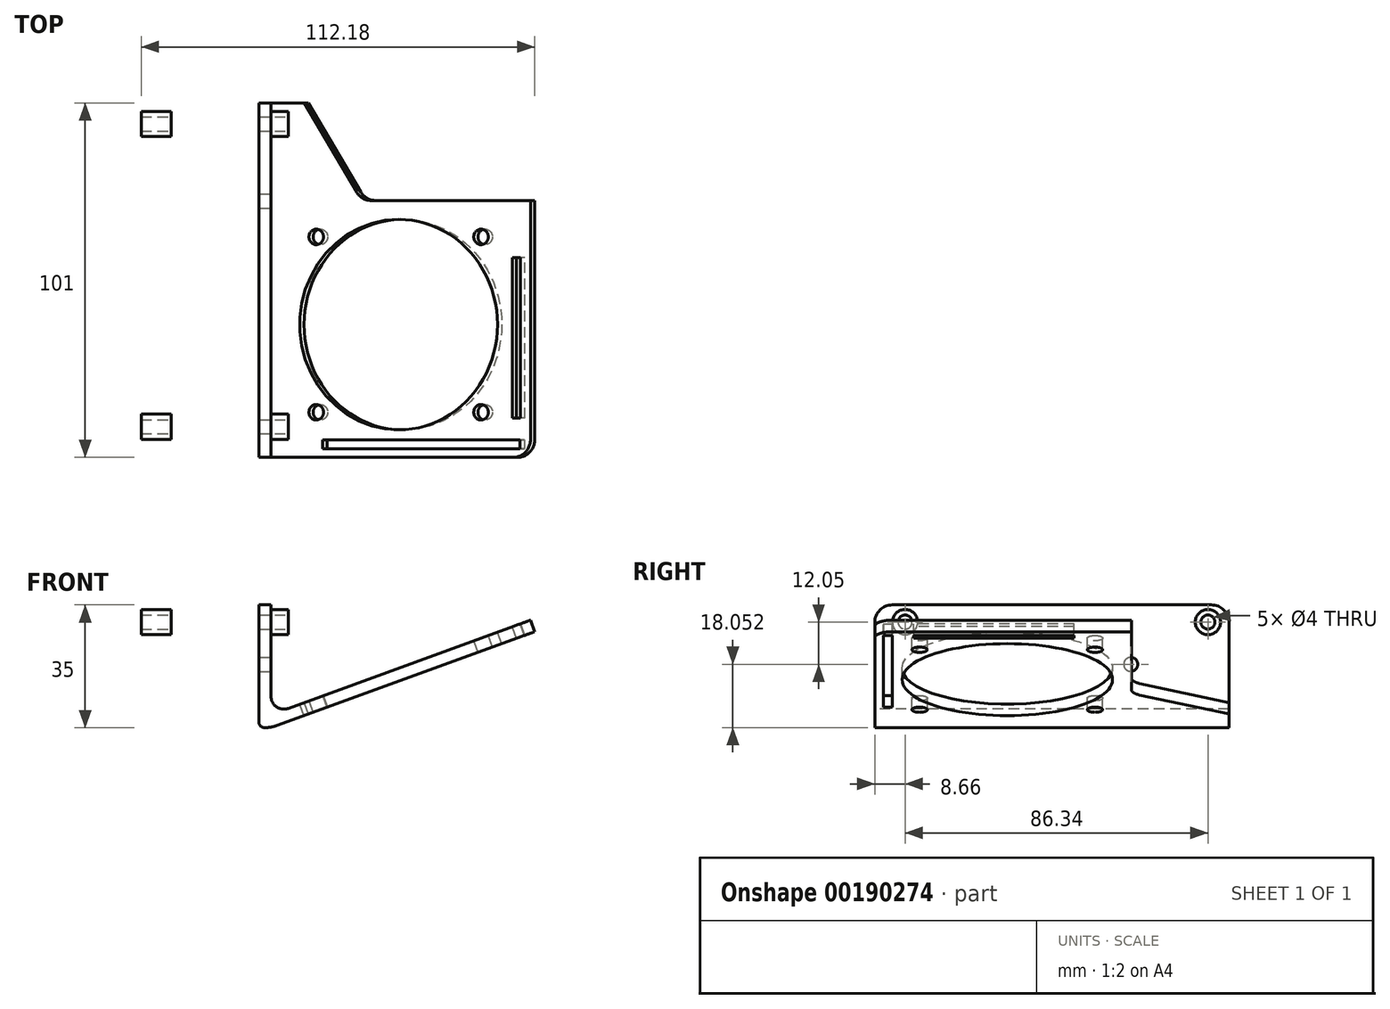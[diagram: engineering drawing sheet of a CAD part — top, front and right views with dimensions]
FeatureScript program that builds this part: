
annotation { "Feature Type Name" : "Feature", "Feature Type Description" : "" }
export const myFeature = defineFeature(function(context is Context, id is Id, definition is map)
    precondition{}
    {
        {
            var Q0;
            Q0=qCreatedBy(makeId("Front.planeOp"),FACE);
            var sketch = newSketch(context, id + "F0", { "sketchPlane" : qUnion([Q0])});
            skLineSegment(sketch, "E0.bottom", {"start": v(1.7, 0) * mm, "end": v(1.77, 0) * mm});
            skLineSegment(sketch, "E0.top", {"start": v(0, 35) * mm, "end": v(3.5, 35) * mm});
            skLineSegment(sketch, "E0.left", {"start": v(0, 1.7) * mm, "end": v(0, 35) * mm});
            skLineSegment(sketch, "E0.right", {"start": v(3.5, 8.92) * mm, "end": v(3.5, 35) * mm});
            skLineSegment(sketch, "E1", {"start": v(5.13, 0.6) * mm, "end": v(78.68, 27.36) * mm});
            skLineSegment(sketch, "E2", {"start": v(8.38, 5.5) * mm, "end": v(77.48, 30.65) * mm});
            skLineSegment(sketch, "E3", {"start": v(78.68, 27.36) * mm, "end": v(77.48, 30.65) * mm});
            skPoint(sketch, "E4.visualSharp", {"position": v(3.5, 0) * mm});
            skArc(sketch, "E4.filletArc", {"start": v(1.77, 0) * mm, "mid": v(3.47, 0.15) * mm, "end": v(5.13, 0.6) * mm});
            skPoint(sketch, "E5.visualSharp", {"position": v(0, 0) * mm});
            skArc(sketch, "E5.filletArc", {"start": v(0, 1.7) * mm, "mid": v(0.5, 0.5) * mm, "end": v(1.7, 0) * mm});
            skPoint(sketch, "E6.visualSharp", {"position": v(3.5, 3.72) * mm});
            skArc(sketch, "E6.filletArc", {"start": v(3.5, 8.92) * mm, "mid": v(5.05, 5.94) * mm, "end": v(8.38, 5.5) * mm});
            skSolve(sketch);
        }
        {
            var Q0;
            Q0=makeQuery(id+"F0.imprint","IMPRINT",FACE,{"disambiguationData":[TD([[makeQuery(id+"F0.imprint","IMPRINT",EDGE,{"derivedFrom":sQuery(id+"F0.wireOp",EDGE,"E0.bottom")}),1.0]])]});
            extrude(context, id + "F1", {"entities" : qUnion([Q0]), "oppositeDirection" : true, "depth" : 101 * mm});
        }
        {
            var Q0;
            Q0=makeQuery(id+"F1.opExtrude","SWEPT_FACE",FACE,{"disambiguationData":[OSD([sQuery(id+"F0.wireOp",EDGE,"E0.right")])]});
            var sketch = newSketch(context, id + "F2", { "sketchPlane" : qUnion([Q0])});
            skPoint(sketch, "E7", {"position": v(8.66, 30.1) * mm});
            skPoint(sketch, "E8", {"position": v(95, 30.1) * mm});
            skCircle(sketch, "E9", {"center": v(8.66, 30.1) * mm, "radius": 2 * mm});
            skCircle(sketch, "E10", {"center": v(95, 30.1) * mm, "radius": 2 * mm});
            skCircle(sketch, "E11", {"center": v(73, 18.05) * mm, "radius": 2 * mm});
            skLineSegment(sketch, "E12.bottom", {"start": v(87.7, 12.98) * mm, "end": v(80.04, 12.98) * mm});
            skLineSegment(sketch, "E12.top", {"start": v(87.7, 30.63) * mm, "end": v(80.04, 30.63) * mm});
            skLineSegment(sketch, "E12.left", {"start": v(90.4, 15.68) * mm, "end": v(90.4, 27.93) * mm});
            skLineSegment(sketch, "E12.right", {"start": v(77.34, 15.68) * mm, "end": v(77.34, 27.93) * mm});
            skLineSegment(sketch, "E13.bottom", {"start": v(63.68, 30.09) * mm, "end": v(17.8, 30.09) * mm});
            skLineSegment(sketch, "E13.top", {"start": v(63.68, 12.86) * mm, "end": v(17.8, 12.86) * mm});
            skLineSegment(sketch, "E13.left", {"start": v(66.38, 27.39) * mm, "end": v(66.38, 15.56) * mm});
            skLineSegment(sketch, "E13.right", {"start": v(15.1, 27.39) * mm, "end": v(15.1, 15.56) * mm});
            skPoint(sketch, "E14.visualSharp", {"position": v(90.4, 12.98) * mm});
            skArc(sketch, "E14.filletArc", {"start": v(87.7, 12.98) * mm, "mid": v(89.6, 13.78) * mm, "end": v(90.4, 15.68) * mm});
            skPoint(sketch, "E15.visualSharp", {"position": v(77.34, 12.98) * mm});
            skArc(sketch, "E15.filletArc", {"start": v(77.34, 15.68) * mm, "mid": v(78.13, 13.78) * mm, "end": v(80.04, 12.98) * mm});
            skPoint(sketch, "E16.visualSharp", {"position": v(77.34, 30.63) * mm});
            skArc(sketch, "E16.filletArc", {"start": v(80.04, 30.63) * mm, "mid": v(78.13, 29.84) * mm, "end": v(77.34, 27.93) * mm});
            skPoint(sketch, "E17.visualSharp", {"position": v(90.4, 30.63) * mm});
            skArc(sketch, "E17.filletArc", {"start": v(90.4, 27.93) * mm, "mid": v(89.6, 29.84) * mm, "end": v(87.7, 30.63) * mm});
            skPoint(sketch, "E18.visualSharp", {"position": v(66.38, 12.86) * mm});
            skArc(sketch, "E18.filletArc", {"start": v(63.68, 12.86) * mm, "mid": v(65.59, 13.65) * mm, "end": v(66.38, 15.56) * mm});
            skPoint(sketch, "E19.visualSharp", {"position": v(66.38, 30.09) * mm});
            skArc(sketch, "E19.filletArc", {"start": v(66.38, 27.39) * mm, "mid": v(65.59, 29.3) * mm, "end": v(63.68, 30.09) * mm});
            skPoint(sketch, "E20.visualSharp", {"position": v(15.1, 30.09) * mm});
            skArc(sketch, "E20.filletArc", {"start": v(17.8, 30.09) * mm, "mid": v(15.9, 29.3) * mm, "end": v(15.1, 27.39) * mm});
            skPoint(sketch, "E21.visualSharp", {"position": v(15.1, 12.86) * mm});
            skArc(sketch, "E21.filletArc", {"start": v(15.1, 15.56) * mm, "mid": v(15.9, 13.65) * mm, "end": v(17.8, 12.86) * mm});
            skSolve(sketch);
        }
        {
            var Q0;
            Q0=makeQuery(id+"F2.imprint","IMPRINT",FACE,{"disambiguationData":[TD([[makeQuery(id+"F2.imprint","IMPRINT",EDGE,{"derivedFrom":sQuery(id+"F2.wireOp",EDGE,"E10")}),1.0]])]});
            var Q1;
            Q1=makeQuery(id+"F2.imprint","IMPRINT",FACE,{"disambiguationData":[TD([[makeQuery(id+"F2.imprint","IMPRINT",EDGE,{"derivedFrom":sQuery(id+"F2.wireOp",EDGE,"E11")}),1.0]])]});
            var Q2;
            Q2=makeQuery(id+"F2.imprint","IMPRINT",FACE,{"disambiguationData":[TD([[makeQuery(id+"F2.imprint","IMPRINT",EDGE,{"derivedFrom":sQuery(id+"F2.wireOp",EDGE,"E9")}),1.0]])]});
            extrude(context, id + "F3", {"entities" : qUnion([Q0, Q1, Q2]), "operationType" : NewBodyOperationType.REMOVE, "endBound" : BoundingType.THROUGH_ALL, "oppositeDirection" : true, "depth" : 25 * mm});
        }
        {
            var Q0;
            Q0=makeQuery(id+"F1.opExtrude","SWEPT_FACE",FACE,{"disambiguationData":[OSD([sQuery(id+"F0.wireOp",EDGE,"E0.right")])]});
            var sketch = newSketch(context, id + "F4", { "sketchPlane" : qUnion([Q0])});
            skCircle(sketch, "E22", {"center": v(8.66, 30.1) * mm, "radius": 3.6 * mm});
            skCircle(sketch, "E23", {"center": v(95, 30.1) * mm, "radius": 3.6 * mm});
            skSolve(sketch);
        }
        {
            var Q0;
            Q0=makeQuery(id+"F4.imprint","IMPRINT",FACE,{"disambiguationData":[TD([[makeQuery(id+"F4.imprint","IMPRINT",EDGE,{"derivedFrom":sQuery(id+"F4.wireOp",EDGE,"E22")}),1.0]])]});
            var Q1;
            Q1=makeQuery(id+"F4.imprint","IMPRINT",FACE,{"disambiguationData":[TD([[makeQuery(id+"F4.imprint","IMPRINT",EDGE,{"derivedFrom":sQuery(id+"F4.wireOp",EDGE,"E23")}),1.0]])]});
            extrude(context, id + "F5", {"entities" : qUnion([Q0, Q1]), "operationType" : NewBodyOperationType.ADD, "depth" : 5 * mm});
        }
        {
            var Q0;
            Q0=makeQuery(id+"F1.opExtrude","SWEPT_FACE",FACE,{"disambiguationData":[OSD([sQuery(id+"F0.wireOp",EDGE,"E2")])]});
            var sketch = newSketch(context, id + "F6", { "sketchPlane" : qUnion([Q0])});
            skPoint(sketch, "E24", {"position": v(68.29, 12.8) * mm});
            skPoint(sketch, "E25", {"position": v(18.29, 12.8) * mm});
            skPoint(sketch, "E26", {"position": v(18.29, 62.8) * mm});
            skPoint(sketch, "E27", {"position": v(68.29, 62.8) * mm});
            skPoint(sketch, "E28", {"position": v(43.29, 37.8) * mm});
            skSolve(sketch);
        }
        {
            var Q0;
            Q0=sQuery(id+"F6.wireOp",VERTEX,"E25");
            var Q1;
            Q1=sQuery(id+"F6.wireOp",VERTEX,"E26");
            var Q2;
            Q2=sQuery(id+"F6.wireOp",VERTEX,"E27");
            var Q3;
            Q3=sQuery(id+"F6.wireOp",VERTEX,"E24");
            var Q4;
            Q4=makeQuery(id+"F1.opExtrude","SWEPT_BODY",BODY,{"disambiguationData":[OSD([sQuery(id+"F0.wireOp",EDGE,"E0.bottom"),sQuery(id+"F0.wireOp",EDGE,"E0.top"),sQuery(id+"F0.wireOp",EDGE,"E0.left"),sQuery(id+"F0.wireOp",EDGE,"E0.right"),sQuery(id+"F0.wireOp",EDGE,"E1"),sQuery(id+"F0.wireOp",EDGE,"E2"),sQuery(id+"F0.wireOp",EDGE,"E3"),sQuery(id+"F0.wireOp",EDGE,"E4.filletArc"),sQuery(id+"F0.wireOp",EDGE,"E5.filletArc"),sQuery(id+"F0.wireOp",EDGE,"E6.filletArc")])]});
            hole(context, id + "F7", {"style" : HoleStyle.SIMPLE, "endStyle" : HoleEndStyle.THROUGH, "holeDiameter" : 4.4 * mm, "startFromSketch" : true, "locations" : qUnion([Q0, Q1, Q2, Q3]), "scope" : qUnion([Q4]), "isTappedThrough" : true});
        }
        {
            var Q0;
            Q0=makeQuery(id+"F1.opExtrude","SWEPT_FACE",FACE,{"disambiguationData":[OSD([sQuery(id+"F0.wireOp",EDGE,"E2")])]});
            var sketch = newSketch(context, id + "F8", { "sketchPlane" : qUnion([Q0])});
            skCircle(sketch, "E29.0", {"center": v(18.29, 62.8) * mm, "radius": 2.2 * mm});
            skCircle(sketch, "E30", {"center": v(43.29, 37.8) * mm, "radius": 30 * mm});
            skSolve(sketch);
        }
        {
            var Q0;
            Q0=makeQuery(id+"F8.imprint","IMPRINT",FACE,{"disambiguationData":[TD([[makeQuery(id+"F8.imprint","IMPRINT",EDGE,{"derivedFrom":sQuery(id+"F8.wireOp",EDGE,"E30")}),1.0]])]});
            extrude(context, id + "F9", {"entities" : qUnion([Q0]), "operationType" : NewBodyOperationType.REMOVE, "endBound" : BoundingType.THROUGH_ALL, "oppositeDirection" : true, "depth" : 25 * mm});
        }
        {
            var Q0;
            Q0=makeQuery(id+"F1.opExtrude","SWEPT_FACE",FACE,{"disambiguationData":[OSD([sQuery(id+"F0.wireOp",EDGE,"E2")])]});
            var sketch = newSketch(context, id + "F10", { "sketchPlane" : qUnion([Q0])});
            skLineSegment(sketch, "E31.bottom", {"start": v(14.62, 101) * mm, "end": v(83.29, 101) * mm});
            skLineSegment(sketch, "E31.top", {"start": v(32.04, 73.18) * mm, "end": v(83.29, 73.18) * mm});
            skLineSegment(sketch, "E31.left", {"start": v(14.62, 101) * mm, "end": v(32.04, 73.18) * mm});
            skLineSegment(sketch, "E31.right", {"start": v(83.29, 101) * mm, "end": v(83.29, 73.18) * mm});
            skLineSegment(sketch, "E32.bottom", {"start": v(77.8, 56.86) * mm, "end": v(80.3, 56.86) * mm});
            skLineSegment(sketch, "E32.top", {"start": v(77.8, 11.12) * mm, "end": v(80.3, 11.12) * mm});
            skLineSegment(sketch, "E32.left", {"start": v(77.8, 56.86) * mm, "end": v(77.8, 11.12) * mm});
            skLineSegment(sketch, "E32.right", {"start": v(80.3, 56.86) * mm, "end": v(80.3, 11.12) * mm});
            skLineSegment(sketch, "E33.bottom", {"start": v(80.16, 2.46) * mm, "end": v(20.29, 2.46) * mm});
            skLineSegment(sketch, "E33.top", {"start": v(80.16, 4.96) * mm, "end": v(20.29, 4.96) * mm});
            skLineSegment(sketch, "E33.left", {"start": v(80.16, 2.46) * mm, "end": v(80.16, 4.96) * mm});
            skLineSegment(sketch, "E33.right", {"start": v(20.29, 2.46) * mm, "end": v(20.29, 4.96) * mm});
            skSolve(sketch);
        }
        {
            var Q0;
            Q0=makeQuery(id+"F10.imprint","IMPRINT",FACE,{"disambiguationData":[TD([[makeQuery(id+"F10.imprint","IMPRINT",EDGE,{"derivedFrom":sQuery(id+"F10.wireOp",EDGE,"E31.bottom")}),-1.0]])]});
            var Q1;
            Q1=makeQuery(id+"F10.imprint","IMPRINT",FACE,{"disambiguationData":[TD([[makeQuery(id+"F10.imprint","IMPRINT",EDGE,{"derivedFrom":sQuery(id+"F10.wireOp",EDGE,"E32.bottom")}),-1.0]])]});
            var Q2;
            Q2=makeQuery(id+"F10.imprint","IMPRINT",FACE,{"disambiguationData":[TD([[makeQuery(id+"F10.imprint","IMPRINT",EDGE,{"derivedFrom":sQuery(id+"F10.wireOp",EDGE,"E33.bottom")}),-1.0]])]});
            extrude(context, id + "F11", {"entities" : qUnion([Q0, Q1, Q2]), "operationType" : NewBodyOperationType.REMOVE, "endBound" : BoundingType.THROUGH_ALL, "oppositeDirection" : true, "depth" : 25 * mm});
        }
        {
            var Q0;
            Q0=makeQuery(id+"F11.boolean.opBoolean","COPY",EDGE,{"derivedFrom":makeQuery(id+"F11.opExtrude","SWEPT_EDGE",EDGE,{"disambiguationData":[OSD([sQuery(id+"F0.wireOp",EDGE,"E2"),sQuery(id+"F10.wireOp",EDGE,"E31.bottom"),sQuery(id+"F10.wireOp",EDGE,"E31.left")])]})});
            var Q1;
            Q1=makeQuery(id+"F11.boolean.opBoolean","COPY",EDGE,{"derivedFrom":makeQuery(id+"F11.opExtrude","SWEPT_EDGE",EDGE,{"disambiguationData":[OSD([sQuery(id+"F10.wireOp",EDGE,"E31.top"),sQuery(id+"F10.wireOp",EDGE,"E31.left")])]})});
            var Q2;
            Q2=makeQuery(id+"F11.boolean.opBoolean","COPY",EDGE,{"derivedFrom":makeQuery(id+"F11.opExtrude","SWEPT_EDGE",EDGE,{"disambiguationData":[OSD([sQuery(id+"F0.wireOp",EDGE,"E2"),sQuery(id+"F0.wireOp",EDGE,"E3"),sQuery(id+"F10.wireOp",EDGE,"E31.top"),sQuery(id+"F10.wireOp",EDGE,"E31.right")])]})});
            var Q3;
            Q3=makeQuery(id+"F1.opExtrude","CAP_EDGE",EDGE,{"disambiguationData":[OSD([sQuery(id+"F0.wireOp",EDGE,"E3")])],"isStart":true});
            var Q4;
            Q4=makeQuery(id+"F1.opExtrude","CAP_EDGE",EDGE,{"disambiguationData":[OSD([sQuery(id+"F0.wireOp",EDGE,"E0.top")])],"isStart":true});
            var Q5;
            Q5=makeQuery(id+"F1.opExtrude","CAP_EDGE",EDGE,{"disambiguationData":[OSD([sQuery(id+"F0.wireOp",EDGE,"E0.top")])],"isStart":false});
            fillet(context, id + "F12", {"entities" : qUnion([Q0, Q1, Q2, Q3, Q4, Q5]), "radius" : 5 * mm, "tangentPropagation" : true, "allowEdgeOverflow" : false});
        }
        {
            var Q0;
            Q0=makeQuery(id+"F1.opExtrude","SWEPT_FACE",FACE,{"disambiguationData":[OSD([sQuery(id+"F0.wireOp",EDGE,"E0.right")])]});
            var sketch = newSketch(context, id + "F13", { "sketchPlane" : qUnion([Q0])});
            skLineSegment(sketch, "E34.bottom", {"start": v(17.06, 31.5) * mm, "end": v(19.06, 31.5) * mm});
            skLineSegment(sketch, "E34.top", {"start": v(17.06, 12.49) * mm, "end": v(19.06, 12.49) * mm});
            skLineSegment(sketch, "E34.left", {"start": v(17.06, 31.5) * mm, "end": v(17.06, 12.49) * mm});
            skLineSegment(sketch, "E34.right", {"start": v(19.06, 31.5) * mm, "end": v(19.06, 12.49) * mm});
            skSolve(sketch);
        }
        {
            var Q0;
            Q0=makeQuery(id+"F1.opExtrude","SWEPT_FACE",FACE,{"disambiguationData":[OSD([sQuery(id+"F0.wireOp",EDGE,"E0.right")])]});
            var sketch = newSketch(context, id + "F14", { "sketchPlane" : qUnion([Q0])});
            skLineSegment(sketch, "E35.bottom", {"start": v(78.64, 29.5) * mm, "end": v(80.64, 29.5) * mm});
            skLineSegment(sketch, "E35.top", {"start": v(78.64, 11.06) * mm, "end": v(80.64, 11.06) * mm});
            skLineSegment(sketch, "E35.left", {"start": v(78.64, 29.5) * mm, "end": v(78.64, 11.06) * mm});
            skLineSegment(sketch, "E35.right", {"start": v(80.64, 29.5) * mm, "end": v(80.64, 11.06) * mm});
            skSolve(sketch);
        }
        {
            var Q0;
            Q0=qCreatedBy(makeId("Right.planeOp"),FACE);
            cPlane(context, id + "F15", {"entities" : qUnion([Q0]), "cplaneType" : CPlaneType.OFFSET, "offset" : 25 * mm, "oppositeDirection" : true, "width" : 150 * mm, "height" : 150 * mm});
        }
        {
            var Q0;
            Q0=qCreatedBy(id+"F15.planeOp",FACE);
            var sketch = newSketch(context, id + "F16", { "sketchPlane" : qUnion([Q0])});
            skCircle(sketch, "E36.0", {"center": v(95, 30.1) * mm, "radius": 2 * mm});
            skCircle(sketch, "E37.0", {"center": v(8.66, 30.1) * mm, "radius": 2 * mm});
            skCircle(sketch, "E38", {"center": v(8.66, 30.1) * mm, "radius": 3.6 * mm});
            skCircle(sketch, "E39", {"center": v(95, 30.1) * mm, "radius": 3.6 * mm});
            skSolve(sketch);
        }
        {
            var Q0;
            Q0=makeQuery(id+"F16.imprint","IMPRINT",FACE,{"disambiguationData":[TD([[makeQuery(id+"F16.imprint","IMPRINT",EDGE,{"derivedFrom":sQuery(id+"F16.wireOp",EDGE,"E36.0")}),-1.0]])]});
            var Q1;
            Q1=makeQuery(id+"F16.imprint","IMPRINT",FACE,{"disambiguationData":[TD([[makeQuery(id+"F16.imprint","IMPRINT",EDGE,{"derivedFrom":sQuery(id+"F16.wireOp",EDGE,"E37.0")}),-1.0]])]});
            extrude(context, id + "F17", {"entities" : qUnion([Q0, Q1]), "operationType" : NewBodyOperationType.ADD, "oppositeDirection" : true, "depth" : 8.5 * mm});
        }
    });
